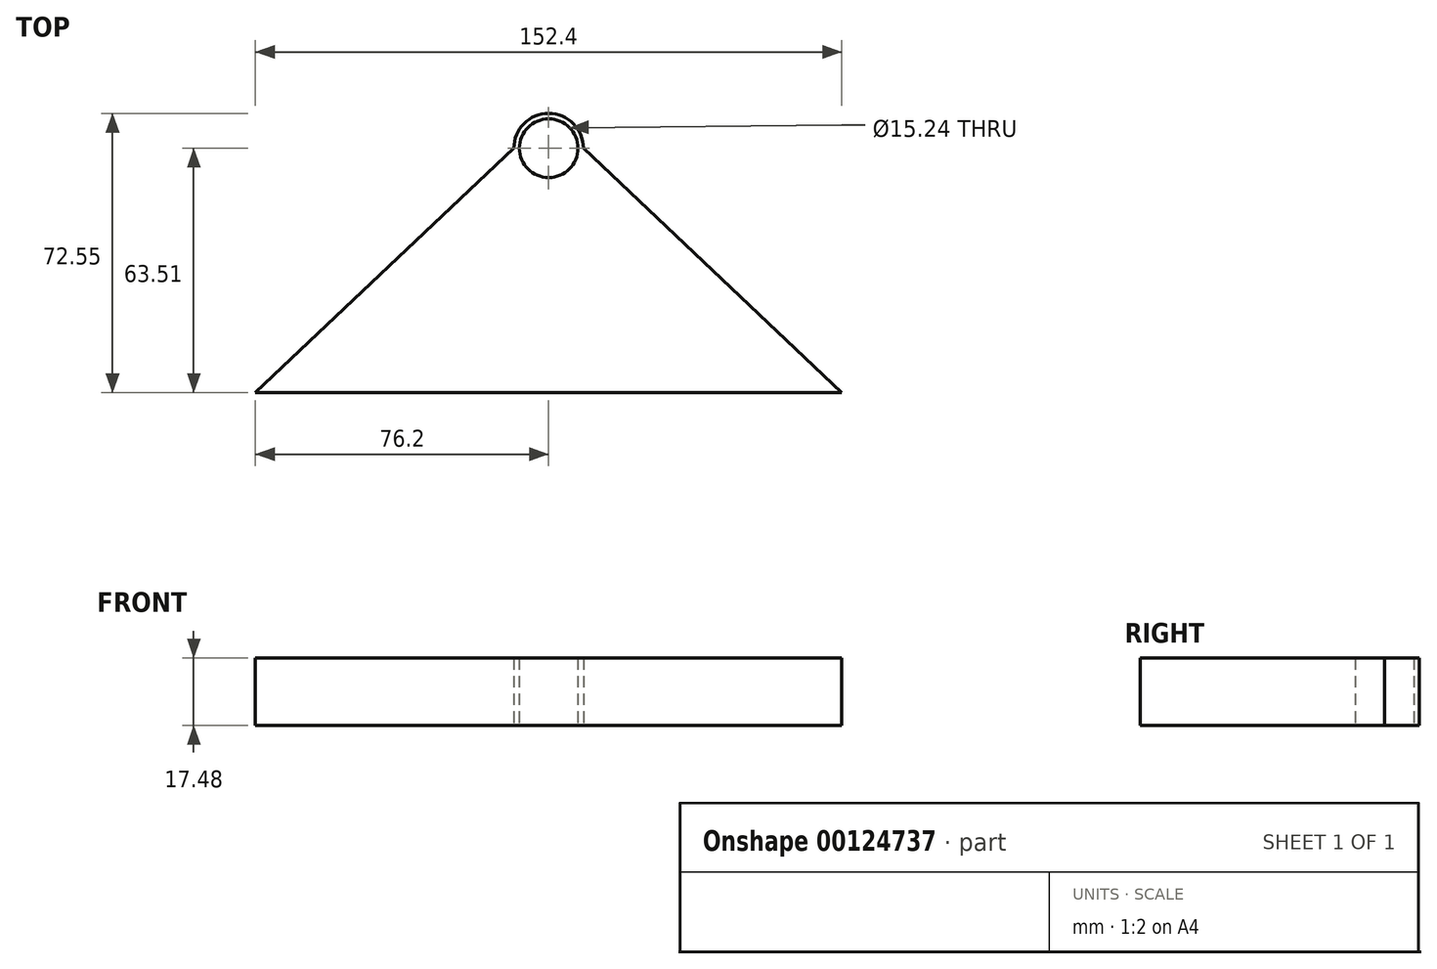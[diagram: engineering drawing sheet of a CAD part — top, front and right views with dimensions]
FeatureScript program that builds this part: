
annotation { "Feature Type Name" : "Feature", "Feature Type Description" : "" }
export const myFeature = defineFeature(function(context is Context, id is Id, definition is map)
    precondition{}
    {
        {
            var Q0;
            Q0=qCreatedBy(makeId("Top.planeOp"),FACE);
            var sketch = newSketch(context, id + "F0", { "sketchPlane" : qUnion([Q0])});
            skCircle(sketch, "E0", {"center": v(0, 0) * mm, "radius": 9.04 * mm});
            skCircle(sketch, "E1", {"center": v(0, 0) * mm, "radius": 7.62 * mm});
            skLineSegment(sketch, "E2", {"start": v(0, 0) * mm, "end": v(0, -63.5) * mm, "construction": true});
            skLineSegment(sketch, "E3", {"start": v(-76.2, -63.5) * mm, "end": v(76.2, -63.5) * mm});
            skLineSegment(sketch, "E4", {"start": v(-9.04, 0) * mm, "end": v(-76.2, -63.5) * mm});
            skLineSegment(sketch, "E5", {"start": v(9.04, 0) * mm, "end": v(76.2, -63.5) * mm});
            skSolve(sketch);
        }
        {
            var Q0;
            Q0=makeQuery(id+"F0.imprint","IMPRINT",FACE,{"disambiguationData":[TD([[makeQuery(id+"F0.imprint","IMPRINT",EDGE,{"derivedFrom":sQuery(id+"F0.wireOp",EDGE,"E3")}),1.0]])]});
            var Q1;
            Q1=makeQuery(id+"F0.imprint","IMPRINT",FACE,{"disambiguationData":[TD([[makeQuery(id+"F0.imprint","IMPRINT",EDGE,{"derivedFrom":sQuery(id+"F0.wireOp",EDGE,"E1")}),-1.0]])]});
            extrude(context, id + "F1", {"entities" : qUnion([Q0, Q1]), "depth" : 17.48 * mm});
        }
    });
